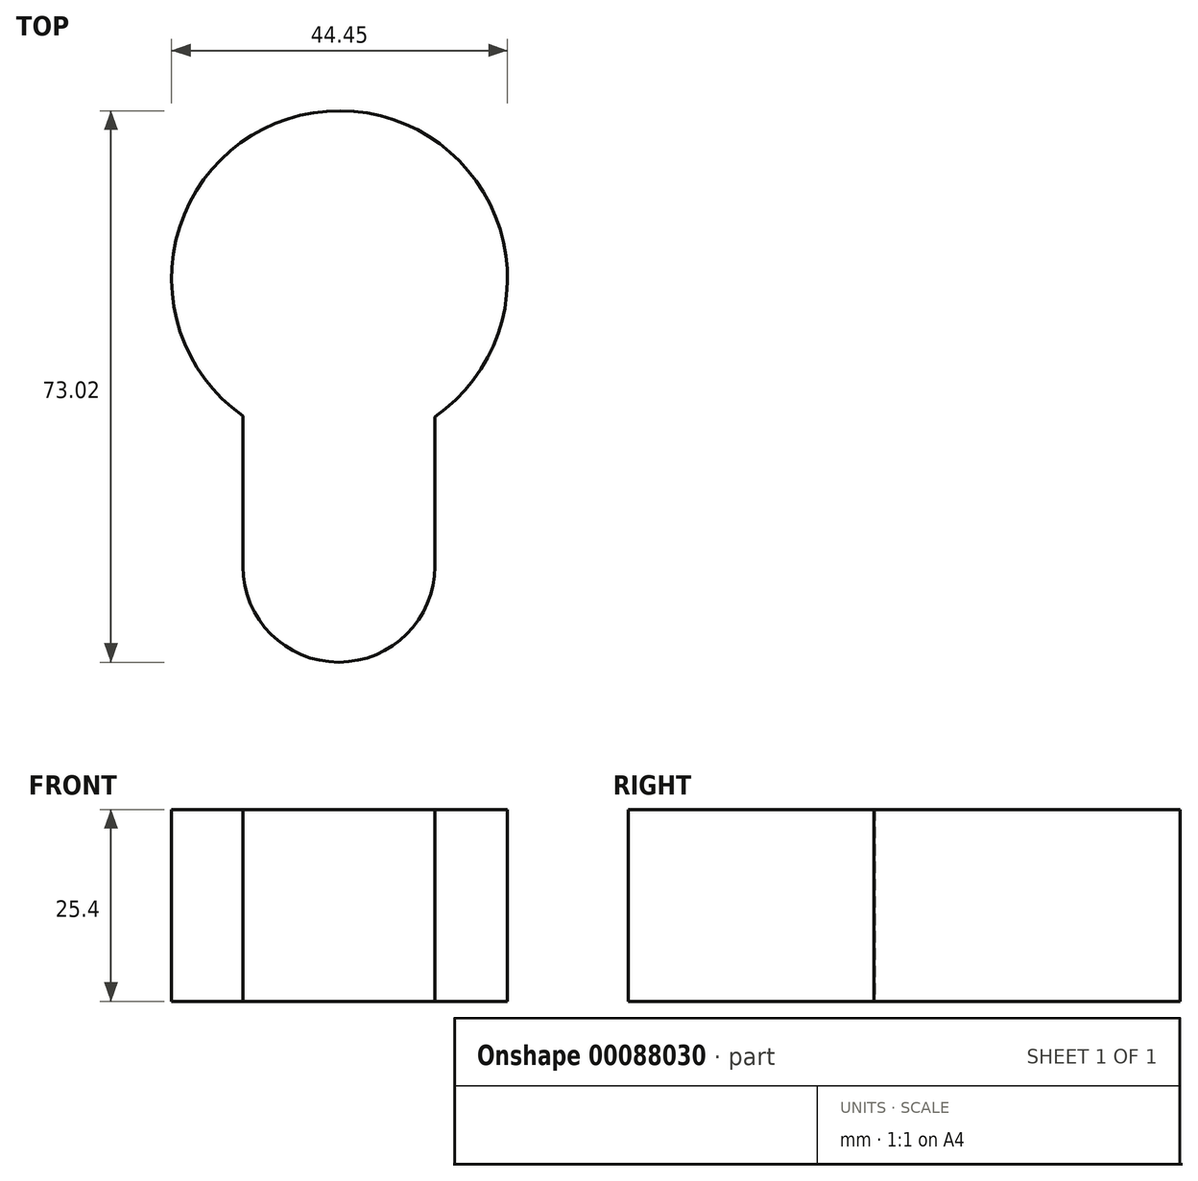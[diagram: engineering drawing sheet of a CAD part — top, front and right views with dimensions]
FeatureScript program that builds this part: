
annotation { "Feature Type Name" : "Feature", "Feature Type Description" : "" }
export const myFeature = defineFeature(function(context is Context, id is Id, definition is map)
    precondition{}
    {
        {
            var Q0;
            Q0=qCreatedBy(makeId("Top.planeOp"),FACE);
            var sketch = newSketch(context, id + "F0", { "sketchPlane" : qUnion([Q0])});
            skArc(sketch, "E0", {"start": v(12.6, -18.3) * mm, "mid": v(0.11, 22.22) * mm, "end": v(-12.8, -18.17) * mm});
            skLineSegment(sketch, "E1", {"start": v(0, 0) * mm, "end": v(0, 22.23) * mm});
            skLineSegment(sketch, "E2", {"start": v(-0.1, -25.4) * mm, "end": v(-0.1, -38.1) * mm});
            skLineSegment(sketch, "E3", {"start": v(0, 0) * mm, "end": v(-0.1, -25.4) * mm});
            skArc(sketch, "E4", {"start": v(-12.8, -38.1) * mm, "mid": v(-0.1, -50.8) * mm, "end": v(12.6, -38.1) * mm});
            skLineSegment(sketch, "E5", {"start": v(-12.8, -18.17) * mm, "end": v(-12.8, -38.1) * mm});
            skLineSegment(sketch, "E6", {"start": v(12.6, -18.3) * mm, "end": v(12.6, -38.1) * mm});
            skSolve(sketch);
        }
        {
            var Q0;
            Q0=makeQuery(id+"F0.imprint","IMPRINT",FACE,{"disambiguationData":[TD([[makeQuery(id+"F0.imprint","IMPRINT",EDGE,{"derivedFrom":sQuery(id+"F0.wireOp",EDGE,"E0")}),1.0]])]});
            extrude(context, id + "F1", {"entities" : qUnion([Q0]), "depth" : 25.4 * mm});
        }
    });
